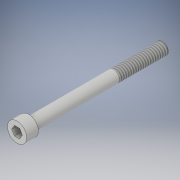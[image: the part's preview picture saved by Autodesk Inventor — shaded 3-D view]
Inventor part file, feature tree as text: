
AUTODESK INVENTOR PART (.ipt)
format: ipt  version: 2018 (Build 220112000, 112)  size: 120,320 bytes
history: native  units: in
note: dims shown in document units (in); Inventor stores cm internally (conversion verified against a paired STEP export)
features: extrude x3, sketch x3, thread x1, fillet x1
ambient origin geometry x8: Origin, YZ Plane, XZ Plane, XY Plane, X Axis, Y Axis, Z Axis, Center Point
bodies: Solid1 (feature_tree)
feature tree (8):
  extrude  "Extrusion1"  Depth=2.3in TaperAngle=0.0deg
  extrude  "Extrusion2"  Depth=0.1562in
  extrude  "Extrusion3"  Depth=0.01in TaperAngle=0.0deg
  thread  "Thread1"  [1 undecoded]
  fillet  "Fillet1"  [1 undecoded]
  sketch  "Sketch1"  dims[d0=0.2031in d1=2.3in d2=0.0in]
  sketch  "Sketch2"  dims[d3=0.2in d4=0.0in d5=0.1562in]
  sketch  "Sketch3"  dims[d6=0.175in d7=0.0in d8=0.85in d9=0.0in d10=0.01in]
note: 2 required parameter values undecoded (feature->parameter linkage not recoverable at this tier; creation-order binding heuristic only, values carry confidence <= 0.55)
